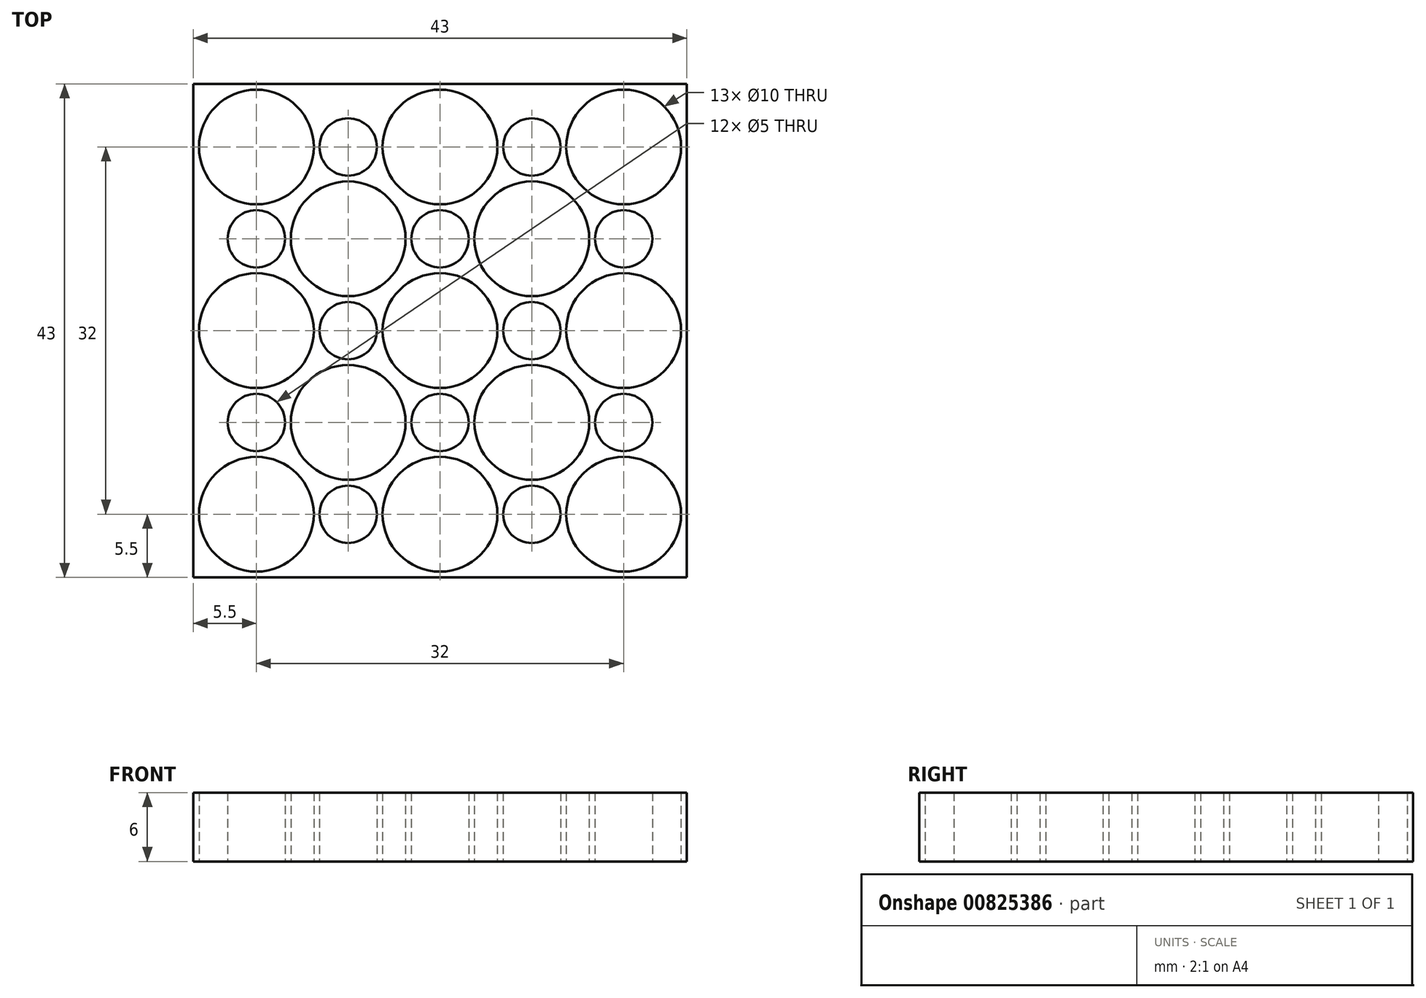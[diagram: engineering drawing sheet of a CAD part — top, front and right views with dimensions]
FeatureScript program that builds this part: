
annotation { "Feature Type Name" : "Feature", "Feature Type Description" : "" }
export const myFeature = defineFeature(function(context is Context, id is Id, definition is map)
    precondition{}
    {
        {
            var Q0;
            Q0=qCreatedBy(makeId("Top.planeOp"),FACE);
            var sketch = newSketch(context, id + "F0", { "sketchPlane" : qUnion([Q0])});
            skCircle(sketch, "E0", {"center": v(0, 0) * mm, "radius": 5 * mm});
            skCircle(sketch, "E1", {"center": v(-8, 0) * mm, "radius": 2.5 * mm});
            skCircle(sketch, "E2", {"center": v(-8, -8) * mm, "radius": 5 * mm});
            skCircle(sketch, "E3", {"center": v(0, -8) * mm, "radius": 2.5 * mm});
            skCircle(sketch, "E4.0.1.0", {"center": v(0, -24) * mm, "radius": 2.5 * mm});
            skCircle(sketch, "E4.0.1.1", {"center": v(-8, -24) * mm, "radius": 5 * mm});
            skCircle(sketch, "E4.0.1.2", {"center": v(-8, -16) * mm, "radius": 2.5 * mm});
            skCircle(sketch, "E4.0.1.3", {"center": v(0, -16) * mm, "radius": 5 * mm});
            skCircle(sketch, "E4.0.2.2", {"center": v(-8, -32) * mm, "radius": 2.5 * mm});
            skCircle(sketch, "E4.0.2.3", {"center": v(0, -32) * mm, "radius": 5 * mm});
            skCircle(sketch, "E4.1.0.0", {"center": v(-16, -8) * mm, "radius": 2.5 * mm});
            skCircle(sketch, "E4.1.0.1", {"center": v(-24, -8) * mm, "radius": 5 * mm});
            skCircle(sketch, "E4.1.0.2", {"center": v(-24, 0) * mm, "radius": 2.5 * mm});
            skCircle(sketch, "E4.1.0.3", {"center": v(-16, 0) * mm, "radius": 5 * mm});
            skCircle(sketch, "E4.1.1.0", {"center": v(-16, -24) * mm, "radius": 2.5 * mm});
            skCircle(sketch, "E4.1.1.1", {"center": v(-24, -24) * mm, "radius": 5 * mm});
            skCircle(sketch, "E4.1.1.2", {"center": v(-24, -16) * mm, "radius": 2.5 * mm});
            skCircle(sketch, "E4.1.1.3", {"center": v(-16, -16) * mm, "radius": 5 * mm});
            skCircle(sketch, "E4.1.2.2", {"center": v(-24, -32) * mm, "radius": 2.5 * mm});
            skCircle(sketch, "E4.1.2.3", {"center": v(-16, -32) * mm, "radius": 5 * mm});
            skCircle(sketch, "E4.2.0.0", {"center": v(-32, -8) * mm, "radius": 2.5 * mm});
            skCircle(sketch, "E4.2.0.3", {"center": v(-32, 0) * mm, "radius": 5 * mm});
            skCircle(sketch, "E4.2.1.0", {"center": v(-32, -24) * mm, "radius": 2.5 * mm});
            skCircle(sketch, "E4.2.1.3", {"center": v(-32, -16) * mm, "radius": 5 * mm});
            skCircle(sketch, "E4.2.2.3", {"center": v(-32, -32) * mm, "radius": 5 * mm});
            skLineSegment(sketch, "E4.direction1", {"start": v(-8, -8) * mm, "end": v(-24, -8) * mm, "construction": true});
            skLineSegment(sketch, "E4.direction2", {"start": v(-8, -8) * mm, "end": v(-8, -24) * mm, "construction": true});
            skLineSegment(sketch, "E5.bottom", {"start": v(5.5, -37.5) * mm, "end": v(-37.5, -37.5) * mm});
            skLineSegment(sketch, "E5.top", {"start": v(5.5, 5.5) * mm, "end": v(-37.5, 5.5) * mm});
            skLineSegment(sketch, "E5.left", {"start": v(5.5, -37.5) * mm, "end": v(5.5, 5.5) * mm});
            skLineSegment(sketch, "E5.right", {"start": v(-37.5, -37.5) * mm, "end": v(-37.5, 5.5) * mm});
            skSolve(sketch);
        }
        {
            var Q0;
            Q0=makeQuery(id+"F0.imprint","IMPRINT",FACE,{"disambiguationData":[TD([[makeQuery(id+"F0.imprint","IMPRINT",EDGE,{"derivedFrom":sQuery(id+"F0.wireOp",EDGE,"E0")}),-1.0]])]});
            extrude(context, id + "F1", {"entities" : qUnion([Q0]), "depth" : 6 * mm, "offsetDistance" : 25 * mm});
        }
    });
